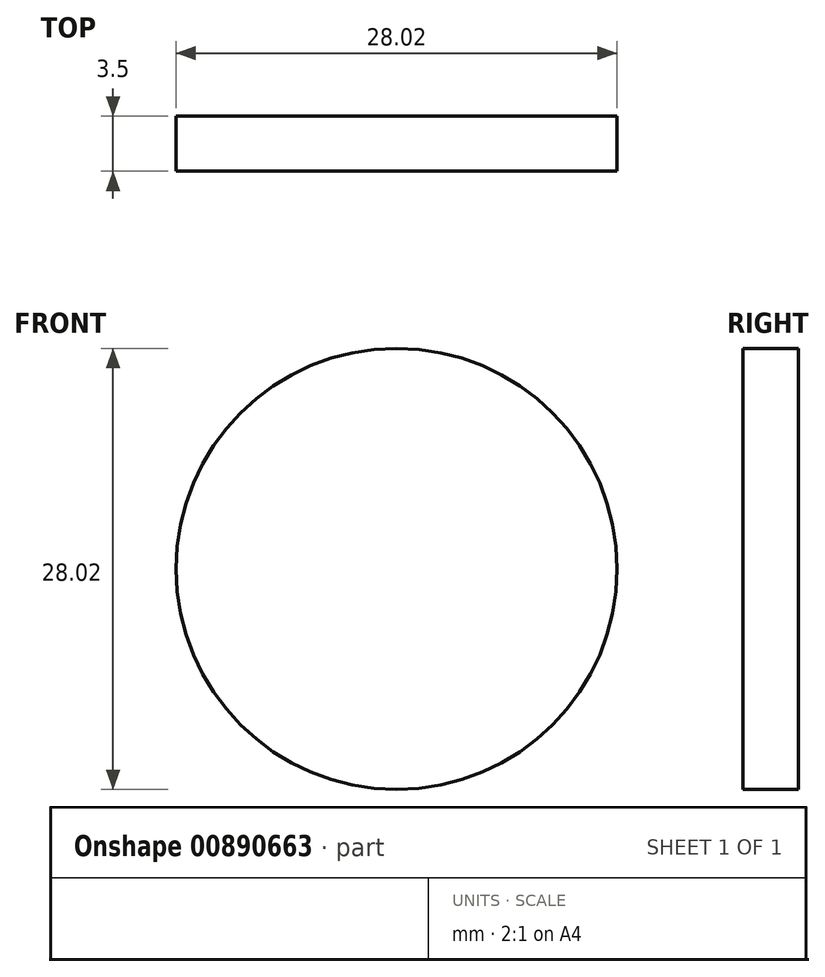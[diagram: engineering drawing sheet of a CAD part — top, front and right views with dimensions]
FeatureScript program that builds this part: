
annotation { "Feature Type Name" : "Feature", "Feature Type Description" : "" }
export const myFeature = defineFeature(function(context is Context, id is Id, definition is map)
    precondition{}
    {
        {
            var Q0;
            Q0=qCreatedBy(makeId("Front.planeOp"),FACE);
            var sketch = newSketch(context, id + "F0", { "sketchPlane" : qUnion([Q0])});
            skCircle(sketch, "E0", {"center": v(0, 0) * mm, "radius": 14 * mm});
            skSolve(sketch);
        }
        {
            var Q0;
            Q0 = qSketchRegion(id + "F0", true);
            extrude(context, id + "F1", {"entities" : qUnion([Q0]), "depth" : 3.5 * mm, "offsetDistance" : 25 * mm});
        }
    });
